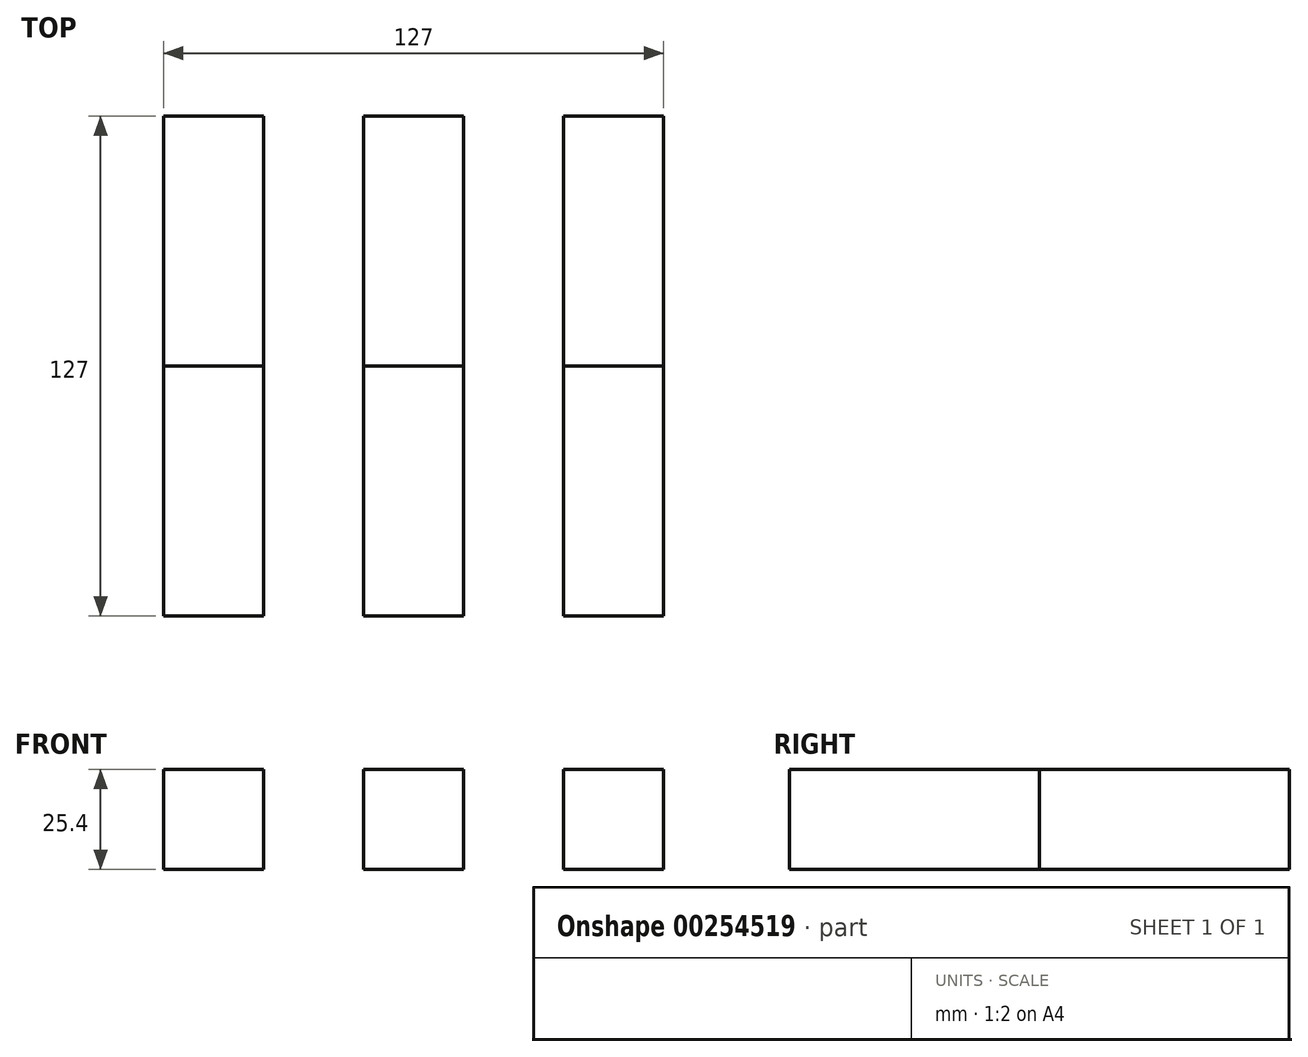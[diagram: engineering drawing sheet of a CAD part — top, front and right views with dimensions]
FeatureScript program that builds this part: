
annotation { "Feature Type Name" : "Feature", "Feature Type Description" : "" }
export const myFeature = defineFeature(function(context is Context, id is Id, definition is map)
    precondition{}
    {
        {
            var Q0;
            Q0=qCreatedBy(makeId("Front.planeOp"),FACE);
            var sketch = newSketch(context, id + "F0", { "sketchPlane" : qUnion([Q0])});
            skLineSegment(sketch, "E0.bottom", {"start": v(12.7, 12.7) * mm, "end": v(-12.7, 12.7) * mm});
            skLineSegment(sketch, "E0.top", {"start": v(12.7, -12.7) * mm, "end": v(-12.7, -12.7) * mm});
            skLineSegment(sketch, "E0.left", {"start": v(12.7, 12.7) * mm, "end": v(12.7, -12.7) * mm});
            skLineSegment(sketch, "E0.right", {"start": v(-12.7, 12.7) * mm, "end": v(-12.7, -12.7) * mm});
            skPoint(sketch, "E0.middle", {"position": v(0, 0) * mm});
            skLineSegment(sketch, "E1.bottom", {"start": v(-50.8, 0) * mm, "end": v(50.8, 0) * mm});
            skLineSegment(sketch, "E1.top", {"start": v(-50.8, 0) * mm, "end": v(50.8, 0) * mm});
            skLineSegment(sketch, "E1.left", {"start": v(-50.8, 0) * mm, "end": v(-50.8, 0) * mm});
            skLineSegment(sketch, "E1.right", {"start": v(50.8, 0) * mm, "end": v(50.8, 0) * mm});
            skLineSegment(sketch, "E2.bottom", {"start": v(-38.1, 12.7) * mm, "end": v(-63.5, 12.7) * mm});
            skLineSegment(sketch, "E2.top", {"start": v(-38.1, -12.7) * mm, "end": v(-63.5, -12.7) * mm});
            skLineSegment(sketch, "E2.left", {"start": v(-38.1, 12.7) * mm, "end": v(-38.1, -12.7) * mm});
            skLineSegment(sketch, "E2.right", {"start": v(-63.5, 12.7) * mm, "end": v(-63.5, -12.7) * mm});
            skPoint(sketch, "E2.middle", {"position": v(-50.8, 0) * mm});
            skLineSegment(sketch, "E3.bottom", {"start": v(38.1, 12.7) * mm, "end": v(63.5, 12.7) * mm});
            skLineSegment(sketch, "E3.top", {"start": v(38.1, -12.7) * mm, "end": v(63.5, -12.7) * mm});
            skLineSegment(sketch, "E3.left", {"start": v(38.1, 12.7) * mm, "end": v(38.1, -12.7) * mm});
            skLineSegment(sketch, "E3.right", {"start": v(63.5, 12.7) * mm, "end": v(63.5, -12.7) * mm});
            skPoint(sketch, "E3.middle", {"position": v(50.8, 0) * mm});
            skLineSegment(sketch, "E4", {"start": v(0, 0) * mm, "end": v(50.8, 0) * mm});
            skSolve(sketch);
        }
        {
            var Q0;
            {var subQ0=sQuery(id+"F0.wireOp",EDGE,"E0.bottom");Q0=makeQuery(id+"F0.imprint","IMPRINT",FACE,{"disambiguationData":[TD([[makeQuery(id+"F0.imprint","IMPRINT",EDGE,{"derivedFrom":subQ0}),1.0]])]});}
            var Q1;
            {var subQ0=sQuery(id+"F0.wireOp",EDGE,"E0.top");Q1=makeQuery(id+"F0.imprint","IMPRINT",FACE,{"disambiguationData":[TD([[makeQuery(id+"F0.imprint","IMPRINT",EDGE,{"derivedFrom":subQ0}),-1.0]])]});}
            var Q2;
            {var subQ3=sQuery(id+"F0.wireOp",EDGE,"E2.bottom");Q2=makeQuery(id+"F0.imprint","IMPRINT",FACE,{"disambiguationData":[TD([[makeQuery(id+"F0.imprint","IMPRINT",EDGE,{"derivedFrom":subQ3}),1.0]])]});}
            var Q3;
            {var subQ3=sQuery(id+"F0.wireOp",EDGE,"E3.bottom");Q3=makeQuery(id+"F0.imprint","IMPRINT",FACE,{"disambiguationData":[TD([[makeQuery(id+"F0.imprint","IMPRINT",EDGE,{"derivedFrom":subQ3}),-1.0]])]});}
            extrude(context, id + "F1", {"entities" : qUnion([Q0, Q1, Q2, Q3]), "depth" : 63.5 * mm});
        }
        {
            var Q0;
            Q0=makeQuery(id+"F1.opExtrude","CAP_FACE",FACE,{"disambiguationData":[OSD([sQuery(id+"F0.wireOp",EDGE,"E3.bottom"),sQuery(id+"F0.wireOp",EDGE,"E3.top"),sQuery(id+"F0.wireOp",EDGE,"E3.left"),sQuery(id+"F0.wireOp",EDGE,"E3.right")])],"isStart":true});
            var Q1;
            Q1=makeQuery(id+"F1.opExtrude","CAP_FACE",FACE,{"disambiguationData":[OSD([sQuery(id+"F0.wireOp",EDGE,"E0.bottom"),sQuery(id+"F0.wireOp",EDGE,"E0.top"),sQuery(id+"F0.wireOp",EDGE,"E0.left"),sQuery(id+"F0.wireOp",EDGE,"E0.right")])],"isStart":true});
            var Q2;
            Q2=makeQuery(id+"F1.opExtrude","CAP_FACE",FACE,{"disambiguationData":[OSD([sQuery(id+"F0.wireOp",EDGE,"E2.bottom"),sQuery(id+"F0.wireOp",EDGE,"E2.top"),sQuery(id+"F0.wireOp",EDGE,"E2.left"),sQuery(id+"F0.wireOp",EDGE,"E2.right")])],"isStart":true});
            extrude(context, id + "F2", {"entities" : qUnion([Q0, Q1, Q2]), "depth" : 63.5 * mm});
        }
    });
